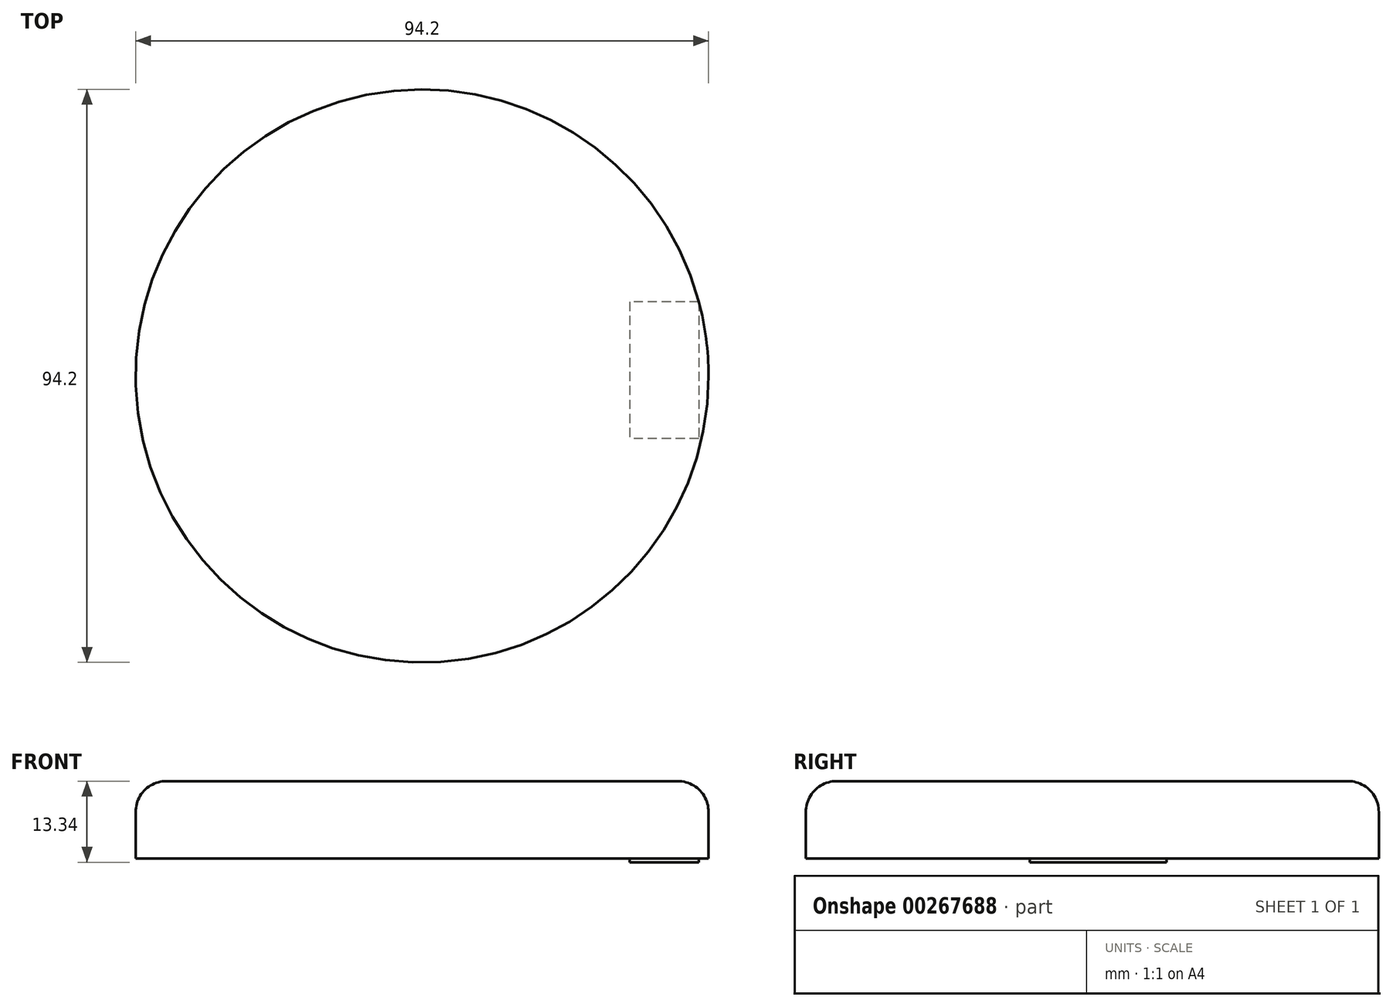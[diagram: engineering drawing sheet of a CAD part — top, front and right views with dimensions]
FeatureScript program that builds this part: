
annotation { "Feature Type Name" : "Feature", "Feature Type Description" : "" }
export const myFeature = defineFeature(function(context is Context, id is Id, definition is map)
    precondition{}
    {
        {
            var Q0;
            Q0=qCreatedBy(makeId("Top.planeOp"),FACE);
            var sketch = newSketch(context, id + "F0", { "sketchPlane" : qUnion([Q0])});
            skCircle(sketch, "E0", {"center": v(0, 0) * mm, "radius": 47.1 * mm});
            skLineSegment(sketch, "E1.bottom", {"start": v(45.5, 12.17) * mm, "end": v(34.11, 12.17) * mm});
            skLineSegment(sketch, "E1.top", {"start": v(45.5, -10.3) * mm, "end": v(34.11, -10.3) * mm});
            skLineSegment(sketch, "E1.left", {"start": v(45.5, 12.17) * mm, "end": v(45.5, -10.3) * mm});
            skLineSegment(sketch, "E1.right", {"start": v(34.11, 12.17) * mm, "end": v(34.11, -10.3) * mm});
            skSolve(sketch);
        }
        {
            var Q0;
            Q0=makeQuery(id+"F0.imprint","IMPRINT",FACE,{"disambiguationData":[TD([[makeQuery(id+"F0.imprint","IMPRINT",EDGE,{"derivedFrom":sQuery(id+"F0.wireOp",EDGE,"E0")}),1.0]])]});
            var Q1;
            Q1=makeQuery(id+"F0.imprint","IMPRINT",FACE,{"disambiguationData":[TD([[makeQuery(id+"F0.imprint","IMPRINT",EDGE,{"derivedFrom":sQuery(id+"F0.wireOp",EDGE,"E1.bottom")}),1.0]])]});
            extrude(context, id + "F1", {"entities" : qUnion([Q0, Q1]), "depth" : 12.7 * mm});
        }
        {
            var Q0;
            Q0=makeQuery(id+"F1.opExtrude","CAP_EDGE",EDGE,{"disambiguationData":[OSD([sQuery(id+"F0.wireOp",EDGE,"E0")])],"isStart":false});
            fillet(context, id + "F2", {"entities" : qUnion([Q0]), "radius" : 5.08 * mm, "tangentPropagation" : true, "allowEdgeOverflow" : false});
        }
        {
            var Q0;
            Q0=makeQuery(id+"F0.imprint","IMPRINT",FACE,{"disambiguationData":[TD([[makeQuery(id+"F0.imprint","IMPRINT",EDGE,{"derivedFrom":sQuery(id+"F0.wireOp",EDGE,"E1.bottom")}),1.0]])]});
            extrude(context, id + "F3", {"entities" : qUnion([Q0]), "operationType" : NewBodyOperationType.ADD, "oppositeDirection" : true, "depth" : 0.64 * mm});
        }
    });
